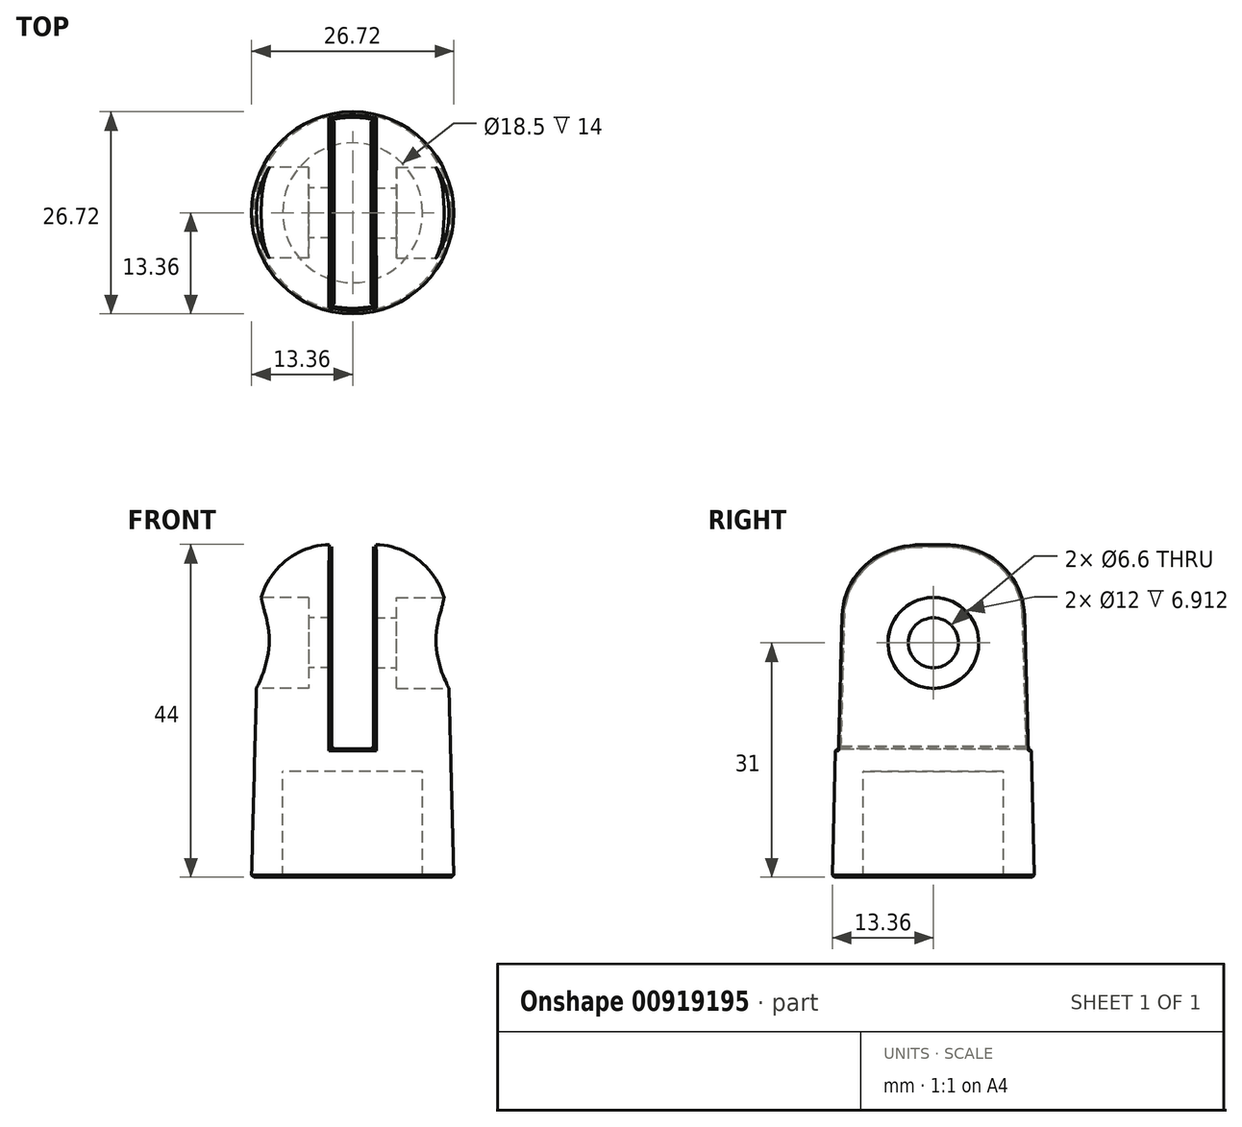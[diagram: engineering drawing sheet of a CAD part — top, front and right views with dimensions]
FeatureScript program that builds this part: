
annotation { "Feature Type Name" : "Feature", "Feature Type Description" : "" }
export const myFeature = defineFeature(function(context is Context, id is Id, definition is map)
    precondition{}
    {
        {
            var Q0;
            Q0=qCreatedBy(makeId("Top.planeOp"),FACE);
            var sketch = newSketch(context, id + "F0", { "sketchPlane" : qUnion([Q0])});
            skCircle(sketch, "E0", {"center": v(0, 0) * mm, "radius": 13 * mm});
            skCircle(sketch, "E1", {"center": v(0, 0) * mm, "radius": 9.5 * mm});
            skSolve(sketch);
        }
        {
            var Q0;
            Q0=makeQuery(id+"F0.imprint","IMPRINT",FACE,{"disambiguationData":[TD([[makeQuery(id+"F0.imprint","IMPRINT",EDGE,{"derivedFrom":sQuery(id+"F0.wireOp",EDGE,"E0")}),1.0]])]});
            var Q1;
            Q1=makeQuery(id+"F0.imprint","IMPRINT",FACE,{"disambiguationData":[TD([[makeQuery(id+"F0.imprint","IMPRINT",EDGE,{"derivedFrom":sQuery(id+"F0.wireOp",EDGE,"E1")}),1.0]])]});
            extrude(context, id + "F1", {"entities" : qUnion([Q0, Q1]), "oppositeDirection" : true, "depth" : 14 * mm, "offsetDistance" : 25 * mm, "hasDraft" : true, "draftAngle" : 1.5 * degree});
        }
        {
            var Q0;
            Q0 = qSketchRegion(id + "F0", true);
            var Q1;
            Q1=makeQuery(id+"F0.imprint","IMPRINT",FACE,{"disambiguationData":[TD([[makeQuery(id+"F0.imprint","IMPRINT",EDGE,{"derivedFrom":sQuery(id+"F0.wireOp",EDGE,"E1")}),1.0]])]});
            extrude(context, id + "F2", {"entities" : qUnion([Q0, Q1]), "operationType" : NewBodyOperationType.ADD, "depth" : 30 * mm, "offsetDistance" : 25 * mm, "hasDraft" : true, "draftAngle" : 1.5 * degree, "draftPullDirection" : true});
        }
        {
            var Q0;
            Q0=qCreatedBy(makeId("Top.planeOp"),FACE);
            cPlane(context, id + "F3", {"entities" : qUnion([Q0]), "cplaneType" : CPlaneType.OFFSET, "offset" : 3 * mm, "width" : 150 * mm, "height" : 150 * mm});
        }
        {
            var Q0;
            Q0=qCreatedBy(id+"F3.planeOp",FACE);
            var sketch = newSketch(context, id + "F4", { "sketchPlane" : qUnion([Q0])});
            skLineSegment(sketch, "E2.bottom", {"start": v(-2.75, 14.76) * mm, "end": v(2.75, 14.76) * mm});
            skLineSegment(sketch, "E2.top", {"start": v(-2.75, -15.24) * mm, "end": v(2.75, -15.24) * mm});
            skLineSegment(sketch, "E2.left", {"start": v(-2.75, 14.76) * mm, "end": v(-2.75, -15.24) * mm});
            skLineSegment(sketch, "E2.right", {"start": v(2.75, 14.76) * mm, "end": v(2.75, -15.24) * mm});
            skSolve(sketch);
        }
        {
            var Q0;
            Q0=makeQuery(id+"F4.imprint","IMPRINT",FACE,{"disambiguationData":[TD([[makeQuery(id+"F4.imprint","IMPRINT",EDGE,{"derivedFrom":sQuery(id+"F4.wireOp",EDGE,"E2.bottom")}),-1.0]])]});
            extrude(context, id + "F5", {"entities" : qUnion([Q0]), "operationType" : NewBodyOperationType.REMOVE, "depth" : 30 * mm, "offsetDistance" : 25 * mm});
        }
        {
            var Q0;
            {var subQ0=sQuery(id+"F0.wireOp",EDGE,"E0");Q0=makeQuery(id+"F5.boolean.opBoolean","SPLIT",EDGE,{"disambiguationData":[TD([makeQuery(id+"F5.opExtrude","SWEPT_FACE",FACE,{"disambiguationData":[OSD([sQuery(id+"F4.wireOp",EDGE,"E2.left")])]})])],"derivedFrom":makeQuery(id+"F2.opExtrude","CAP_EDGE",EDGE,{"disambiguationData":[OSD([subQ0])],"isStart":false})});}
            var Q1;
            {var subQ0=sQuery(id+"F0.wireOp",EDGE,"E0");Q1=makeQuery(id+"F5.boolean.opBoolean","SPLIT",EDGE,{"disambiguationData":[TD([makeQuery(id+"F5.opExtrude","SWEPT_FACE",FACE,{"disambiguationData":[OSD([sQuery(id+"F4.wireOp",EDGE,"E2.right")])]})])],"derivedFrom":makeQuery(id+"F2.opExtrude","CAP_EDGE",EDGE,{"disambiguationData":[OSD([subQ0])],"isStart":false})});}
            fillet(context, id + "F6", {"entities" : qUnion([Q0, Q1]), "radius" : 9.7 * mm, "tangentPropagation" : true, "allowEdgeOverflow" : false});
        }
        {
            var Q0;
            Q0=makeQuery(id+"F5.boolean.opBoolean","INTERSECT",EDGE,{"derivedFrom":[makeQuery(id+"F2.opExtrude","CAP_FACE",FACE,{"disambiguationData":[OSD([sQuery(id+"F0.wireOp",EDGE,"E0")])],"isStart":false}),makeQuery(id+"F5.opExtrude","SWEPT_FACE",FACE,{"disambiguationData":[OSD([sQuery(id+"F4.wireOp",EDGE,"E2.right")])]})]});
            var Q1;
            Q1=makeQuery(id+"F5.boolean.opBoolean","INTERSECT",EDGE,{"derivedFrom":[makeQuery(id+"F2.opExtrude","CAP_FACE",FACE,{"disambiguationData":[OSD([sQuery(id+"F0.wireOp",EDGE,"E0")])],"isStart":false}),makeQuery(id+"F5.opExtrude","SWEPT_FACE",FACE,{"disambiguationData":[OSD([sQuery(id+"F4.wireOp",EDGE,"E2.left")])]})]});
            chamfer(context, id + "F7", {"entities" : qUnion([Q0, Q1]), "width" : 0.3 * mm, "tangentPropagation" : true});
        }
        {
            var Q0;
            Q0=makeQuery(id+"F5.boolean.opBoolean","COPY",EDGE,{"derivedFrom":makeQuery(id+"F5.opExtrude","CAP_EDGE",EDGE,{"disambiguationData":[OSD([sQuery(id+"F4.wireOp",EDGE,"E2.right")])],"isStart":true})});
            var Q1;
            Q1=makeQuery(id+"F5.boolean.opBoolean","COPY",EDGE,{"derivedFrom":makeQuery(id+"F5.opExtrude","CAP_EDGE",EDGE,{"disambiguationData":[OSD([sQuery(id+"F4.wireOp",EDGE,"E2.left")])],"isStart":true})});
            var Q2;
            {var subQ0=sQuery(id+"F0.wireOp",EDGE,"E0");Q2=makeQuery(id+"F5.boolean.opBoolean","INTERSECT",EDGE,{"disambiguationData":[OD(1.0)],"derivedFrom":[makeQuery(id+"F2.boolean.opBoolean","MERGE",FACE,{"derivedFrom":[makeQuery(id+"F1.opExtrude","SWEPT_FACE",FACE,{"disambiguationData":[OSD([subQ0])]}),makeQuery(id+"F2.opExtrude","SWEPT_FACE",FACE,{"disambiguationData":[OSD([subQ0])]})]}),makeQuery(id+"F5.opExtrude","CAP_FACE",FACE,{"disambiguationData":[OSD([sQuery(id+"F4.wireOp",EDGE,"E2.bottom"),sQuery(id+"F4.wireOp",EDGE,"E2.top"),sQuery(id+"F4.wireOp",EDGE,"E2.left"),sQuery(id+"F4.wireOp",EDGE,"E2.right")])],"isStart":true})]});}
            var Q3;
            {var subQ0=sQuery(id+"F0.wireOp",EDGE,"E0");Q3=makeQuery(id+"F5.boolean.opBoolean","INTERSECT",EDGE,{"disambiguationData":[OD(0.0)],"derivedFrom":[makeQuery(id+"F2.boolean.opBoolean","MERGE",FACE,{"derivedFrom":[makeQuery(id+"F1.opExtrude","SWEPT_FACE",FACE,{"disambiguationData":[OSD([subQ0])]}),makeQuery(id+"F2.opExtrude","SWEPT_FACE",FACE,{"disambiguationData":[OSD([subQ0])]})]}),makeQuery(id+"F5.opExtrude","CAP_FACE",FACE,{"disambiguationData":[OSD([sQuery(id+"F4.wireOp",EDGE,"E2.bottom"),sQuery(id+"F4.wireOp",EDGE,"E2.top"),sQuery(id+"F4.wireOp",EDGE,"E2.left"),sQuery(id+"F4.wireOp",EDGE,"E2.right")])],"isStart":true})]});}
            var Q4;
            Q4=makeQuery(id+"F1.opExtrude","CAP_EDGE",EDGE,{"disambiguationData":[OSD([sQuery(id+"F0.wireOp",EDGE,"E0")])],"isStart":false});
            chamfer(context, id + "F8", {"entities" : qUnion([Q0, Q1, Q2, Q3, Q4]), "width" : 0.3 * mm, "tangentPropagation" : true});
        }
        {
            var Q0;
            Q0=qCreatedBy(makeId("Right.planeOp"),FACE);
            cPlane(context, id + "F9", {"entities" : qUnion([Q0]), "cplaneType" : CPlaneType.OFFSET, "offset" : 12.8 * mm, "oppositeDirection" : true, "width" : 150 * mm, "height" : 150 * mm});
        }
        {
            var Q0;
            Q0=qCreatedBy(makeId("Right.planeOp"),FACE);
            cPlane(context, id + "F10", {"entities" : qUnion([Q0]), "cplaneType" : CPlaneType.OFFSET, "offset" : 12.8 * mm, "width" : 150 * mm, "height" : 150 * mm});
        }
        {
            var Q0;
            Q0=qCreatedBy(id+"F9.planeOp",FACE);
            var sketch = newSketch(context, id + "F11", { "sketchPlane" : qUnion([Q0])});
            skPoint(sketch, "E3", {"position": v(0, 17) * mm});
            skSolve(sketch);
        }
        {
            var Q0;
            Q0=qCreatedBy(id+"F10.planeOp",FACE);
            var sketch = newSketch(context, id + "F12", { "sketchPlane" : qUnion([Q0])});
            skPoint(sketch, "E4", {"position": v(0, 17) * mm});
            skSolve(sketch);
        }
        {
            var Q0;
            Q0=sQuery(id+"F11.wireOp",VERTEX,"E3");
            var Q1;
            Q1=makeQuery(id+"F1.opExtrude","SWEPT_BODY",BODY,{"disambiguationData":[OSD([sQuery(id+"F0.wireOp",EDGE,"E0"),sQuery(id+"F0.wireOp",EDGE,"E1")])]});
            hole(context, id + "F13", {"style" : HoleStyle.C_BORE, "endStyle" : HoleEndStyle.BLIND, "oppositeDirection" : true, "holeDiameter" : 6.6 * mm, "cBoreDiameter" : 12 * mm, "cBoreDepth" : 7 * mm, "majorDiameter" : 5 * mm, "holeDepth" : 14.4 * mm, "isTappedThrough" : true, "tappedDepth" : 12 * mm, "tapClearance" : 3, "startFromSketch" : true, "locations" : qUnion([Q0]), "scope" : qUnion([Q1])});
        }
        {
            var Q0;
            Q0=sQuery(id+"F12.wireOp",VERTEX,"E4");
            var Q1;
            Q1=makeQuery(id+"F1.opExtrude","SWEPT_BODY",BODY,{"disambiguationData":[OSD([sQuery(id+"F0.wireOp",EDGE,"E0"),sQuery(id+"F0.wireOp",EDGE,"E1")])]});
            hole(context, id + "F14", {"style" : HoleStyle.C_BORE, "endStyle" : HoleEndStyle.BLIND, "holeDiameter" : 6.6 * mm, "cBoreDiameter" : 12 * mm, "cBoreDepth" : 7 * mm, "majorDiameter" : 5 * mm, "holeDepth" : 14.4 * mm, "isTappedThrough" : true, "tappedDepth" : 12 * mm, "tapClearance" : 3, "startFromSketch" : true, "locations" : qUnion([Q0]), "scope" : qUnion([Q1])});
        }
        {
            var Q0;
            Q0=sQuery(id+"F0.wireOp",VERTEX,"E0.center");
            var Q1;
            Q1=makeQuery(id+"F1.opExtrude","SWEPT_BODY",BODY,{"disambiguationData":[OSD([sQuery(id+"F0.wireOp",EDGE,"E0")])]});
            hole(context, id + "F15", {"style" : HoleStyle.SIMPLE, "endStyle" : HoleEndStyle.BLIND, "holeDiameter" : 18.5 * mm, "majorDiameter" : 5 * mm, "holeDepth" : 15 * mm, "isTappedThrough" : true, "tappedDepth" : 12 * mm, "tapClearance" : 3, "startFromSketch" : true, "locations" : qUnion([Q0]), "scope" : qUnion([Q1])});
        }
    });
